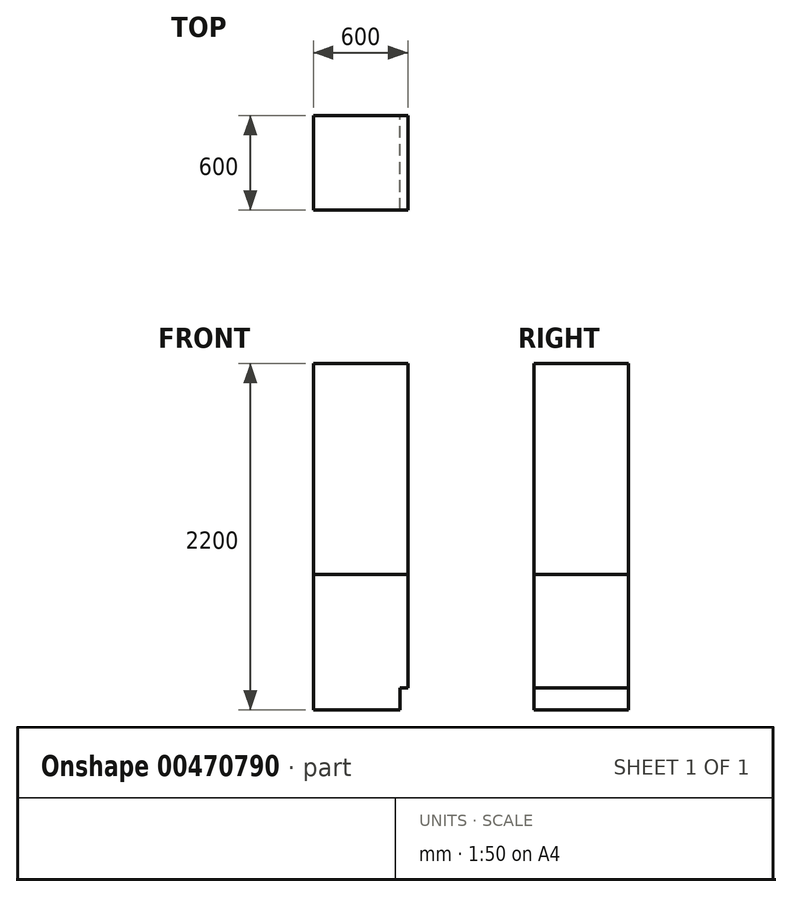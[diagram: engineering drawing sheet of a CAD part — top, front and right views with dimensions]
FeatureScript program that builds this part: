
annotation { "Feature Type Name" : "Feature", "Feature Type Description" : "" }
export const myFeature = defineFeature(function(context is Context, id is Id, definition is map)
    precondition{}
    {
        {
            var Q0;
            Q0=qCreatedBy(makeId("Front.planeOp"),FACE);
            var sketch = newSketch(context, id + "F0", { "sketchPlane" : qUnion([Q0])});
            skLineSegment(sketch, "E0", {"start": v(0, 0) * mm, "end": v(0, 2200) * mm});
            skLineSegment(sketch, "E1", {"start": v(0, 2200) * mm, "end": v(600, 2200) * mm});
            skLineSegment(sketch, "E2", {"start": v(600, 2200) * mm, "end": v(600, 140) * mm});
            skLineSegment(sketch, "E3", {"start": v(600, 140) * mm, "end": v(550, 140) * mm});
            skLineSegment(sketch, "E4", {"start": v(550, 140) * mm, "end": v(550, 0) * mm});
            skLineSegment(sketch, "E5", {"start": v(550, 0) * mm, "end": v(0, 0) * mm});
            skLineSegment(sketch, "E6", {"start": v(0, 860) * mm, "end": v(600, 860) * mm});
            skSolve(sketch);
        }
        {
            var Q0;
            {var subQ0=sQuery(id+"F0.wireOp",EDGE,"E3");Q0=makeQuery(id+"F0.imprint","IMPRINT",FACE,{"disambiguationData":[TD([[makeQuery(id+"F0.imprint","IMPRINT",EDGE,{"derivedFrom":subQ0}),-1.0]])]});}
            extrude(context, id + "F1", {"entities" : qUnion([Q0]), "depth" : 600 * mm});
        }
        {
            var Q0;
            {var subQ0=sQuery(id+"F0.wireOp",EDGE,"E1");Q0=makeQuery(id+"F0.imprint","IMPRINT",FACE,{"disambiguationData":[TD([[makeQuery(id+"F0.imprint","IMPRINT",EDGE,{"derivedFrom":subQ0}),-1.0]])]});}
            var Q1;
            {var subQ0=sQuery(id+"F0.wireOp",EDGE,"E3");Q1=makeQuery(id+"F0.imprint","IMPRINT",FACE,{"disambiguationData":[TD([[makeQuery(id+"F0.imprint","IMPRINT",EDGE,{"derivedFrom":subQ0}),-1.0]])]});}
            extrude(context, id + "F2", {"entities" : qUnion([Q0, Q1]), "depth" : 600 * mm});
        }
    });
